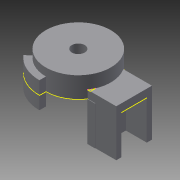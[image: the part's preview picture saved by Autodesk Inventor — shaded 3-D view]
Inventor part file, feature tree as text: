
AUTODESK INVENTOR PART (.ipt)
format: ipt  version: 2013 (Build 170138000, 138)  size: 209,920 bytes
history: native  units: mm
features: sketch x12, extrude x9, other x1, hole x1
ambient origin geometry x8: Origin, YZ Plane, XZ Plane, XY Plane, X Axis, Y Axis, Z Axis, Center Point
feature tree (23):
  other  "ソリッド1"
  extrude  "押し出し1"  Depth=9.768mm
  extrude  "押し出し2"  Depth=15.0mm
  extrude  "押し出し3"  Depth=2.0mm
  extrude  "押し出し4"  Depth=18.0mm
  sketch  "スケッチ5"
  extrude  "押し出し5"  Depth=13.768mm
  extrude  "押し出し6"  Depth=10.0mm TaperAngle=0.0deg
  extrude  "押し出し7"  Depth=2.0mm
  sketch  "スケッチ9"
  extrude  "押し出し8"  Depth=2.0mm
  extrude  "押し出し9"  Depth=12.5mm
  hole  "穴1"  [1 undecoded]
  sketch  "スケッチ1"
  sketch  "スケッチ2"
  sketch  "スケッチ3"
  sketch  "スケッチ4"
  sketch  "スケッチ6"
  sketch  "スケッチ7"
  sketch  "スケッチ8"
  sketch  "スケッチ10"
  sketch  "スケッチ11"
  sketch  "スケッチ12"
note: 1 required parameter value undecoded (feature->parameter linkage not recoverable at this tier; creation-order binding heuristic only, values carry confidence <= 0.55)
